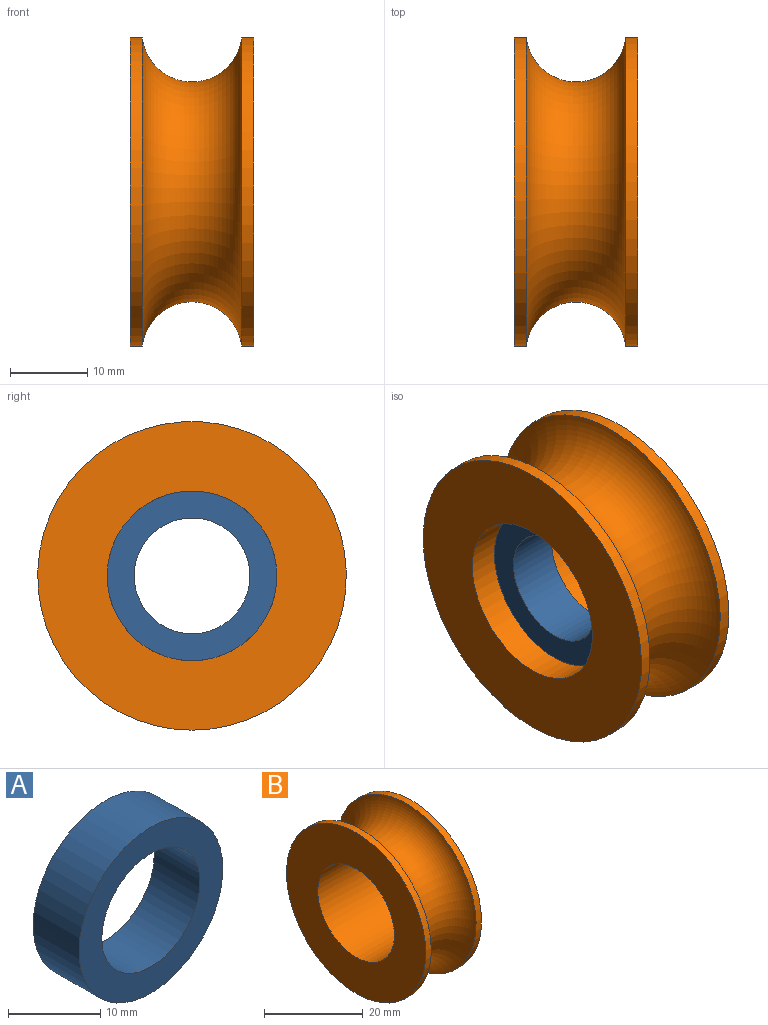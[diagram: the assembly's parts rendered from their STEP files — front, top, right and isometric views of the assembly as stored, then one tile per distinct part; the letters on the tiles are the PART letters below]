
ASSEMBLY  parts=2 mates=1
PART A: 4 faces, bbox 22x7x22 mm
  f0: cylinder r=7.5mm len=15mm, axis (0,1,0), area 329.9mm2, adj f2,f3
  f1: cylinder r=11mm len=22mm, axis (0,1,0), area 483.8mm2, adj f2,f3
  f2: plane 22x22mm, normal (0,-1,0), area 203.4mm2, adj f0,f1
  f3: plane 22x22mm, normal (0,1,0), area 203.4mm2, adj f0,f1
PART B: 6 faces, bbox 16x44.9x44.9 mm
  f0: cylinder r=20mm len=40mm, axis (1,0,0), area 196.7mm2, adj f1,f4
  f1: plane 40x40mm, normal (-1,0,0), area 876.5mm2, adj f0,f5
  f2: plane 40x40mm, normal (1,0,0), area 876.5mm2, adj f3,f5
  f3: cylinder r=20mm len=40mm, axis (1,0,0), area 196.7mm2, adj f2,f4
  f4: torus R=20.74mm, axis (1,0,0), area 1935.2mm2, adj f0,f3
  f5: cylinder r=11mm len=22mm, axis (1,0,0), area 1105.8mm2, adj f1,f2
PLACE A rot(axis=(0.58,-0.58,0.58),120deg) t=(-3.96,2.04,-0.82)mm
PLACE B t=(0,2.04,-0.82)mm
MATE slider A.f0 <-> B.f4  axis (-1,0,0) through (-3.96,2.04,-0.82)mm
